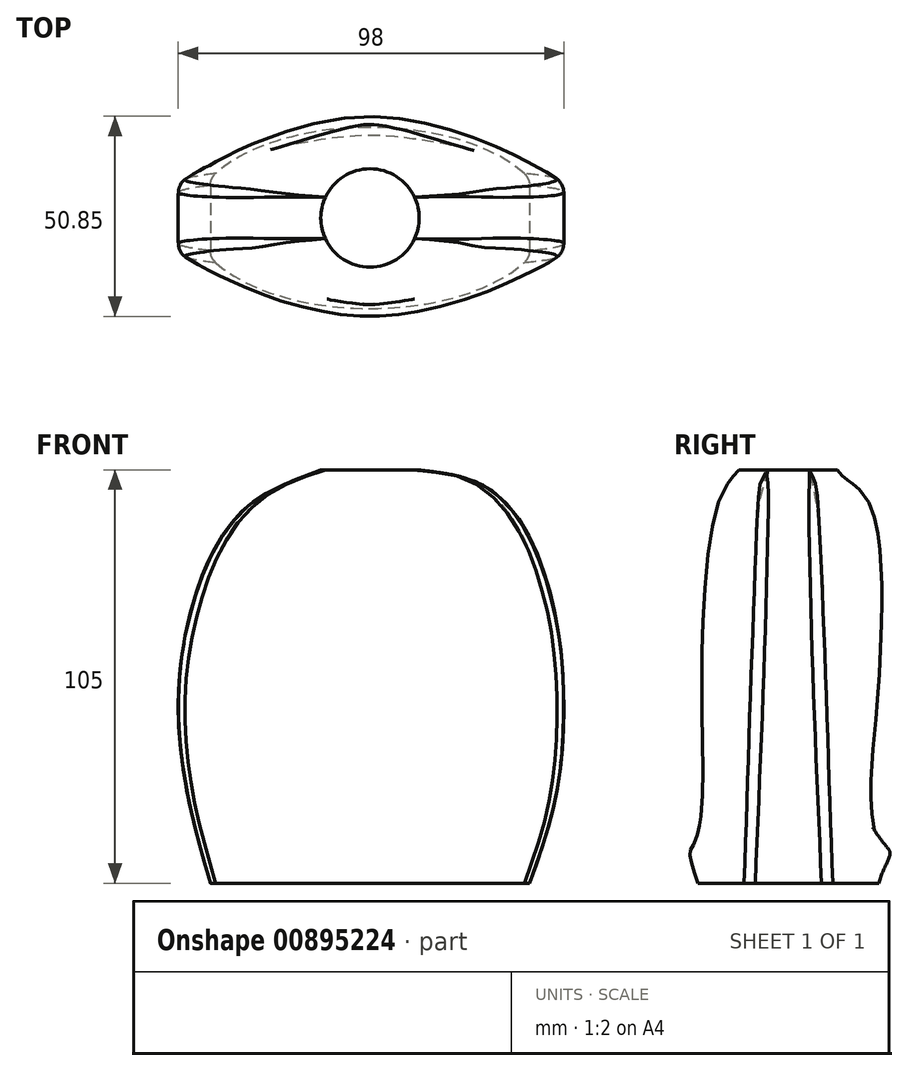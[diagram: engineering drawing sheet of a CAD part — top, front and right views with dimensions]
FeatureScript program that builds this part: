
annotation { "Feature Type Name" : "Feature", "Feature Type Description" : "" }
export const myFeature = defineFeature(function(context is Context, id is Id, definition is map)
    precondition{}
    {
        {
            var Q0;
            Q0=qCreatedBy(makeId("Top.planeOp"),FACE);
            var sketch = newSketch(context, id + "F0", { "sketchPlane" : qUnion([Q0])});
            skLineSegment(sketch, "E0.top", {"start": v(0, 23) * mm, "end": v(45, 23) * mm, "construction": true});
            skLineSegment(sketch, "E0.right", {"start": v(45, 0) * mm, "end": v(45, 23) * mm, "construction": true});
            skEllipticalArc(sketch, "E1", {});
            skLineSegment(sketch, "E2", {"start": v(40.52, 10) * mm, "end": v(40.52, -10) * mm});
            skLineSegment(sketch, "E3.MirrorCS", {"start": v(-40.52, 10) * mm, "end": v(-40.52, -10) * mm});
            skEllipticalArc(sketch, "E4.trimOffspring", {});
            skLineSegment(sketch, "E5", {"start": v(0, 0) * mm, "end": v(0, -23) * mm, "construction": true});
            const initialGuessF0  = {"E1": [0, 0, 1, 0, 0.045, 0.023, 0.44979686042435796, 2.6917957931654355], "E4.trimOffspring": [0, 0, 1, 0, 0.045, 0.023, 3.59138951401415, 5.833388446755229]};
            skSetInitialGuess(sketch, initialGuessF0);
            skSolve(sketch);
        }
        {
            var Q0;
            Q0=qCreatedBy(makeId("Top.planeOp"),FACE);
            cPlane(context, id + "F1", {"entities" : qUnion([Q0]), "cplaneType" : CPlaneType.OFFSET, "offset" : 105 * mm, "width" : 150 * mm, "height" : 150 * mm});
        }
        {
            var Q0;
            Q0=qCreatedBy(id+"F1.planeOp",FACE);
            var sketch = newSketch(context, id + "F2", { "sketchPlane" : qUnion([Q0])});
            skArc(sketch, "E6", {"start": v(11.33, 5.28) * mm, "mid": v(0, 12.5) * mm, "end": v(-11.33, 5.28) * mm});
            skLineSegment(sketch, "E7", {"start": v(-12.5, 0) * mm, "end": v(12.5, 0) * mm, "construction": true});
            skLineSegment(sketch, "E8", {"start": v(0, 0) * mm, "end": v(0, -12.5) * mm, "construction": true});
            skArc(sketch, "E9.trimOffspring", {"start": v(-11.33, -5.28) * mm, "mid": v(0, -12.5) * mm, "end": v(11.33, -5.28) * mm});
            skArc(sketch, "E10", {"start": v(11.33, -5.28) * mm, "mid": v(12.5, 0) * mm, "end": v(11.33, 5.28) * mm});
            skArc(sketch, "E11", {"start": v(-11.33, 5.28) * mm, "mid": v(-12.5, 0) * mm, "end": v(-11.33, -5.28) * mm});
            skSolve(sketch);
        }
        {
            var Q0;
            Q0=qCreatedBy(makeId("Front.planeOp"),FACE);
            var sketch = newSketch(context, id + "F3", { "sketchPlane" : qUnion([Q0])});
            skFitSpline(sketch, "E12", {"points": [v(-40.52, 0) * mm, v(-44.14, 11.31) * mm, v(-48.14, 37.81) * mm, v(-48.14, 56.81) * mm, v(-40.64, 81.81) * mm, v(-25.14, 100.81) * mm, v(-12.5, 105) * mm], "startDerivative": vector(-28.76, 75.37) * mm, "endDerivative": vector(92.4, 16.26) * mm});
            skLineSegment(sketch, "E13", {"start": v(0, 0) * mm, "end": v(0, 114.07) * mm, "construction": true});
            skSolve(sketch);
        }
        {
            var Q0;
            Q0=qCreatedBy(makeId("Front.planeOp"),FACE);
            var sketch = newSketch(context, id + "F4", { "sketchPlane" : qUnion([Q0])});
            skFitSpline(sketch, "E14.MirrorCS", {"points": [v(40.52, 0) * mm, v(41.76, 3.24) * mm, v(44.86, 11.36) * mm, v(48.6, 38.49) * mm, v(49.17, 56.66) * mm, v(42.52, 82.33) * mm, v(26.64, 102.51) * mm, v(16.71, 104.26) * mm, v(12.5, 105) * mm]});
            skSolve(sketch);
        }
        {
            var Q0;
            Q0=qCreatedBy(makeId("Right.planeOp"),FACE);
            var sketch = newSketch(context, id + "F5", { "sketchPlane" : qUnion([Q0])});
            skFitSpline(sketch, "E15", {"points": [v(-23, 0) * mm, v(-25, 8) * mm, v(-24, 10) * mm, v(-22, 19) * mm, v(-22, 49) * mm, v(-18, 96) * mm, v(-12.5, 105) * mm], "startDerivative": vector(-26.49, 77.1) * mm, "endDerivative": vector(42.55, 46.08) * mm});
            skSolve(sketch);
        }
        {
            var Q0;
            Q0=qCreatedBy(makeId("Right.planeOp"),FACE);
            var sketch = newSketch(context, id + "F6", { "sketchPlane" : qUnion([Q0])});
            skFitSpline(sketch, "E16.MirrorCS", {"points": [v(23, 0) * mm, v(24.1, 3.2) * mm, v(25.78, 8.1) * mm, v(23.5, 9.98) * mm, v(21, 20.91) * mm, v(22.75, 48.4) * mm, v(20.74, 96.07) * mm, v(14.5, 102.83) * mm, v(12.5, 105) * mm]});
            skSolve(sketch);
        }
        {
            var Q0;
            Q0=sQuery(id+"F3.wireOp",EDGE,"E12");
            var Q1;
            Q1=sQuery(id+"F0.wireOp",EDGE,"E3.MirrorCS");
            var Q2;
            Q2=sQuery(id+"F2.wireOp",EDGE,"E11");
            var Q3;
            Q3=sQuery(id+"F3.wireOp",EDGE,"E12");
            loft(context, id + "F7", {"bodyType" : ToolBodyType.SURFACE, "addSections" : true, "spine" : qUnion([Q0]), "sectionCount" : 4, "wireProfilesArray" : [{ "wireProfileEntities" : qUnion([Q1]) }, { "wireProfileEntities" : qUnion([Q2]) }], "guidesArray" : [{ "guideEntities" : qUnion([Q3]), "guideDerivativeType" : LoftGuideDerivativeType.DEFAULT, "guideDerivativeMagnitude" : 1 }]});
        }
        {
            var Q0;
            Q0=sQuery(id+"F4.wireOp",EDGE,"E14.MirrorCS");
            var Q1;
            Q1=sQuery(id+"F0.wireOp",EDGE,"E2");
            var Q2;
            Q2=sQuery(id+"F2.wireOp",EDGE,"E10");
            loft(context, id + "F8", {"bodyType" : ToolBodyType.SURFACE, "addSections" : true, "spine" : qUnion([Q0]), "sectionCount" : 4, "wireProfilesArray" : [{ "wireProfileEntities" : qUnion([Q1]) }, { "wireProfileEntities" : qUnion([Q2]) }]});
        }
        {
            var Q0;
            Q0=sQuery(id+"F0.wireOp",EDGE,"E4.trimOffspring");
            var Q1;
            Q1=sQuery(id+"F2.wireOp",EDGE,"E9.trimOffspring");
            var Q2;
            Q2=makeQuery(id+"F7.opLoft","SWEPT_EDGE",EDGE,{"disambiguationData":[OSD([sQuery(id+"F0.wireOp",VERTEX,"E3.MirrorCS.end"),sQuery(id+"F2.wireOp",VERTEX,"E11.end")])]});
            var Q3;
            Q3=sQuery(id+"F5.wireOp",EDGE,"E15");
            var Q4;
            Q4=makeQuery(id+"F8.opLoft","SWEPT_EDGE",EDGE,{"disambiguationData":[OSD([sQuery(id+"F0.wireOp",VERTEX,"E2.end"),sQuery(id+"F2.wireOp",VERTEX,"E10.start")])]});
            loft(context, id + "F9", {"bodyType" : ToolBodyType.SURFACE, "surfaceOperationType" : NewSurfaceOperationType.ADD, "addGuides" : true, "wireProfilesArray" : [{ "wireProfileEntities" : qUnion([Q0]) }, { "wireProfileEntities" : qUnion([Q1]) }], "guidesArray" : [{ "guideEntities" : qUnion([Q2]), "guideDerivativeType" : LoftGuideDerivativeType.DEFAULT, "guideDerivativeMagnitude" : 1 }, { "guideEntities" : qUnion([Q3]), "guideDerivativeType" : LoftGuideDerivativeType.DEFAULT, "guideDerivativeMagnitude" : 1 }, { "guideEntities" : qUnion([Q4]), "guideDerivativeType" : LoftGuideDerivativeType.DEFAULT, "guideDerivativeMagnitude" : 1 }]});
        }
        {
            var Q0;
            Q0=sQuery(id+"F0.wireOp",EDGE,"E1");
            var Q1;
            Q1=sQuery(id+"F2.wireOp",EDGE,"E6");
            var Q2;
            Q2=makeQuery(id+"F8.opLoft","SWEPT_EDGE",EDGE,{"disambiguationData":[OSD([sQuery(id+"F0.wireOp",VERTEX,"E2.start"),sQuery(id+"F2.wireOp",VERTEX,"E10.end")])]});
            var Q3;
            Q3=sQuery(id+"F6.wireOp",EDGE,"E16.MirrorCS");
            var Q4;
            Q4=makeQuery(id+"F7.opLoft","SWEPT_EDGE",EDGE,{"disambiguationData":[OSD([sQuery(id+"F0.wireOp",VERTEX,"E3.MirrorCS.start"),sQuery(id+"F2.wireOp",VERTEX,"E11.start")])]});
            loft(context, id + "F10", {"bodyType" : ToolBodyType.SURFACE, "surfaceOperationType" : NewSurfaceOperationType.ADD, "addGuides" : true, "wireProfilesArray" : [{ "wireProfileEntities" : qUnion([Q0]) }, { "wireProfileEntities" : qUnion([Q1]) }], "guidesArray" : [{ "guideEntities" : qUnion([Q2]), "guideDerivativeType" : LoftGuideDerivativeType.DEFAULT, "guideDerivativeMagnitude" : 1 }, { "guideEntities" : qUnion([Q3]), "guideDerivativeType" : LoftGuideDerivativeType.DEFAULT, "guideDerivativeMagnitude" : 1 }, { "guideEntities" : qUnion([Q4]), "guideDerivativeType" : LoftGuideDerivativeType.DEFAULT, "guideDerivativeMagnitude" : 1 }]});
        }
        {
            var Q0;
            Q0=sQuery(id+"F0.wireOp",EDGE,"E4.trimOffspring");
            var Q1;
            Q1=sQuery(id+"F0.wireOp",EDGE,"E1");
            var Q2;
            Q2=sQuery(id+"F0.wireOp",EDGE,"E2");
            var Q3;
            Q3=sQuery(id+"F0.wireOp",EDGE,"E3.MirrorCS");
            loft(context, id + "F11", {"bodyType" : ToolBodyType.SURFACE, "surfaceOperationType" : NewSurfaceOperationType.ADD, "addGuides" : true, "wireProfilesArray" : [{ "wireProfileEntities" : qUnion([Q0]) }, { "wireProfileEntities" : qUnion([Q1]) }], "guidesArray" : [{ "guideEntities" : qUnion([Q2]), "guideDerivativeType" : LoftGuideDerivativeType.DEFAULT, "guideDerivativeMagnitude" : 1 }, { "guideEntities" : qUnion([Q3]), "guideDerivativeType" : LoftGuideDerivativeType.DEFAULT, "guideDerivativeMagnitude" : 1 }]});
        }
        {
            var Q0;
            {var subQ0=sQuery(id+"F2.wireOp",VERTEX,"E10.start");var subQ1=sQuery(id+"F0.wireOp",VERTEX,"E2.end");Q0=makeQuery(id+"F9.join.opBoolean","MERGE",EDGE,{"derivedFrom":[makeQuery(id+"F8.opLoft","SWEPT_EDGE",EDGE,{"disambiguationData":[OSD([subQ1,subQ0])]}),makeQuery(id+"F9.opLoft","SWEPT_EDGE",EDGE,{"disambiguationData":[OSD([subQ1,subQ0])]})]});}
            var Q1;
            {var subQ0=sQuery(id+"F2.wireOp",VERTEX,"E10.end");var subQ1=sQuery(id+"F0.wireOp",VERTEX,"E2.start");Q1=makeQuery(id+"F10.join.opBoolean","MERGE",EDGE,{"derivedFrom":[makeQuery(id+"F8.opLoft","SWEPT_EDGE",EDGE,{"disambiguationData":[OSD([subQ1,subQ0])]}),makeQuery(id+"F10.opLoft","SWEPT_EDGE",EDGE,{"disambiguationData":[OSD([subQ1,subQ0])]})]});}
            var Q2;
            {var subQ0=sQuery(id+"F2.wireOp",VERTEX,"E11.start");var subQ1=sQuery(id+"F0.wireOp",VERTEX,"E3.MirrorCS.start");Q2=makeQuery(id+"F10.join.opBoolean","MERGE",EDGE,{"derivedFrom":[makeQuery(id+"F7.opLoft","SWEPT_EDGE",EDGE,{"disambiguationData":[OSD([subQ1,subQ0])]}),makeQuery(id+"F10.opLoft","SWEPT_EDGE",EDGE,{"disambiguationData":[OSD([subQ1,subQ0])]})]});}
            var Q3;
            {var subQ0=sQuery(id+"F2.wireOp",VERTEX,"E11.end");var subQ1=sQuery(id+"F0.wireOp",VERTEX,"E3.MirrorCS.end");Q3=makeQuery(id+"F9.join.opBoolean","MERGE",EDGE,{"derivedFrom":[makeQuery(id+"F7.opLoft","SWEPT_EDGE",EDGE,{"disambiguationData":[OSD([subQ1,subQ0])]}),makeQuery(id+"F9.opLoft","SWEPT_EDGE",EDGE,{"disambiguationData":[OSD([subQ1,subQ0])]})]});}
            fillet(context, id + "F12", {"entities" : qUnion([Q0, Q1, Q2, Q3]), "radius" : 4 * mm, "tangentPropagation" : true, "allowEdgeOverflow" : false});
        }
    });
